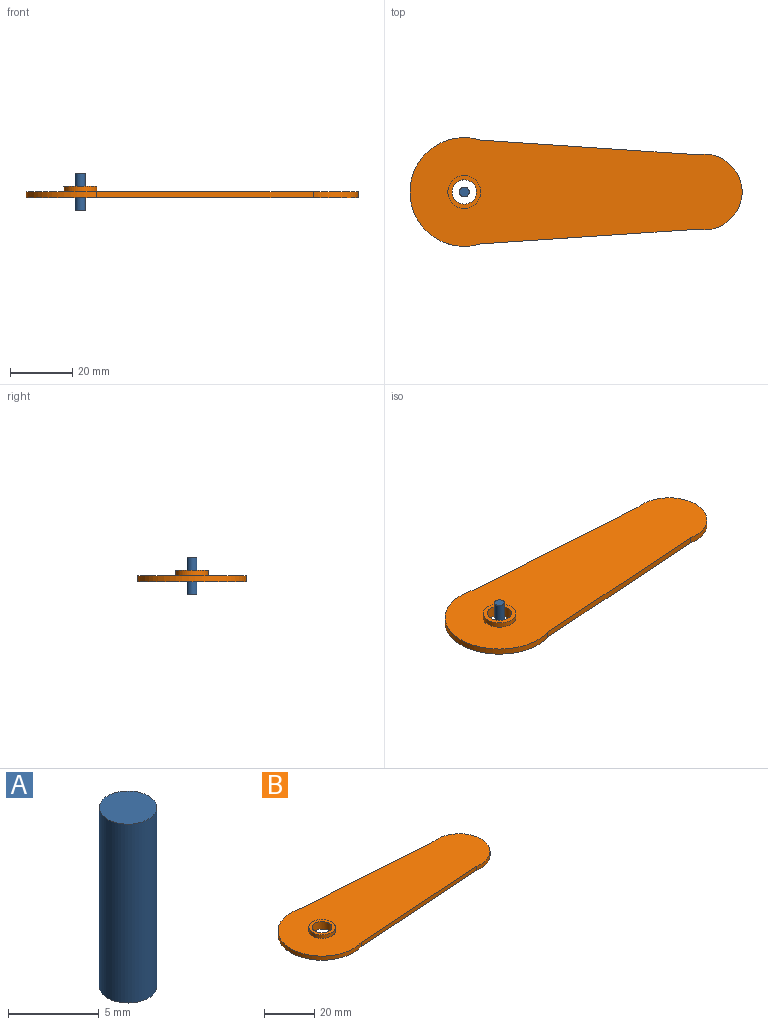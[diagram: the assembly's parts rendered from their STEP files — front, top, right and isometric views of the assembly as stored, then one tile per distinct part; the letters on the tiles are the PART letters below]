
ASSEMBLY  parts=2 mates=1
PART A: 3 faces, bbox 3.2x3.2x12.1 mm
  f0: cylinder r=1.59mm len=12.09mm, axis (0,0,-1), area 120.6mm2, adj f1,f2
  f1: plane 3.18x3.18mm, normal (0,0,1), area 7.9mm2, adj f0
  f2: plane 3.18x3.18mm, normal (0,0,-1), area 7.9mm2, adj f0
PART B: 9 faces, bbox 107x35.1x3.7 mm
  f0: plane 69.68x4.71mm, normal (0.07,1,0), area 140.1mm2, adj f1,f3,f4,f5
  f1: cylinder r=17.53mm len=35.05mm, axis (0,0,-1), area 132mm2, adj f0,f2,f4,f5
  f2: plane 69.68x4.71mm, normal (0.07,-1,0), area 140.1mm2, adj f1,f3,f4,f5
  f3: cylinder r=12.22mm len=24.43mm, axis (0,0,-1), area 86.2mm2, adj f0,f2,f4,f5
  f4: plane 106.99x35.05mm, normal (0,0,1), area 2867.4mm2, adj f0,f1,f2,f3,f6
  f5: plane 106.99x35.05mm, normal (0,0,-1), area 2907.4mm2, adj f0,f1,f2,f3,f8
  f6: cylinder r=5.3mm len=10.59mm, axis (0,0,-1), area 56.6mm2, adj f4,f7
  f7: plane 10.59x10.59mm, normal (0,0,1), area 40mm2, adj f6,f8
  f8: cylinder r=3.91mm len=7.82mm, axis (0,0,1), area 91.1mm2, adj f5,f7
PLACE A t=(-130.87,3.26,-18.99)mm
PLACE B t=(-5.9,8.73,-14.8)mm fixed
MATE cylindrical A.f0 <-> B.f8  axis (0,0,-1) through (-5.9,8.73,-12.95)mm
